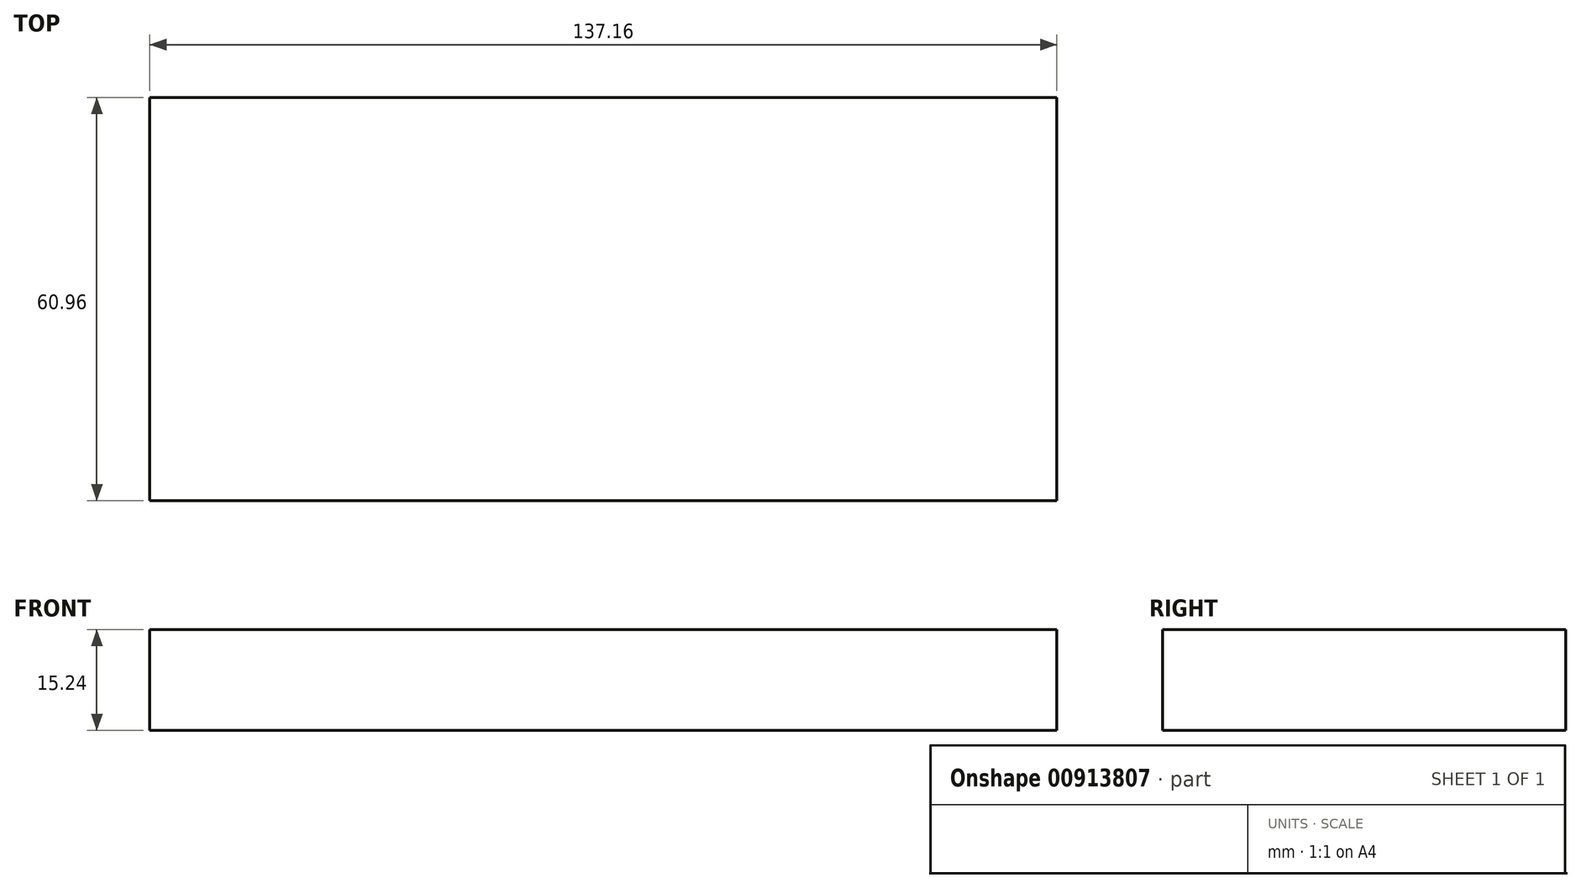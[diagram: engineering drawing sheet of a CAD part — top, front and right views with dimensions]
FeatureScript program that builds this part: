
annotation { "Feature Type Name" : "Feature", "Feature Type Description" : "" }
export const myFeature = defineFeature(function(context is Context, id is Id, definition is map)
    precondition{}
    {
        {
            var Q0;
            Q0=qCreatedBy(makeId("Top.planeOp"),FACE);
            var sketch = newSketch(context, id + "F0", { "sketchPlane" : qUnion([Q0])});
            skLineSegment(sketch, "E0.bottom", {"start": v(-68.58, 30.48) * mm, "end": v(68.58, 30.48) * mm});
            skLineSegment(sketch, "E0.top", {"start": v(-68.58, -30.48) * mm, "end": v(68.58, -30.48) * mm});
            skLineSegment(sketch, "E0.left", {"start": v(-68.58, 30.48) * mm, "end": v(-68.58, -30.48) * mm});
            skLineSegment(sketch, "E0.right", {"start": v(68.58, 30.48) * mm, "end": v(68.58, -30.48) * mm});
            skSolve(sketch);
        }
        {
            var Q0;
            Q0=makeQuery(id+"F0.imprint","IMPRINT",FACE,{"disambiguationData":[TD([[makeQuery(id+"F0.imprint","IMPRINT",EDGE,{"derivedFrom":sQuery(id+"F0.wireOp",EDGE,"E0.bottom")}),-1.0]])]});
            extrude(context, id + "F1", {"entities" : qUnion([Q0]), "depth" : 15.24 * mm, "offsetDistance" : 25.4 * mm});
        }
    });
